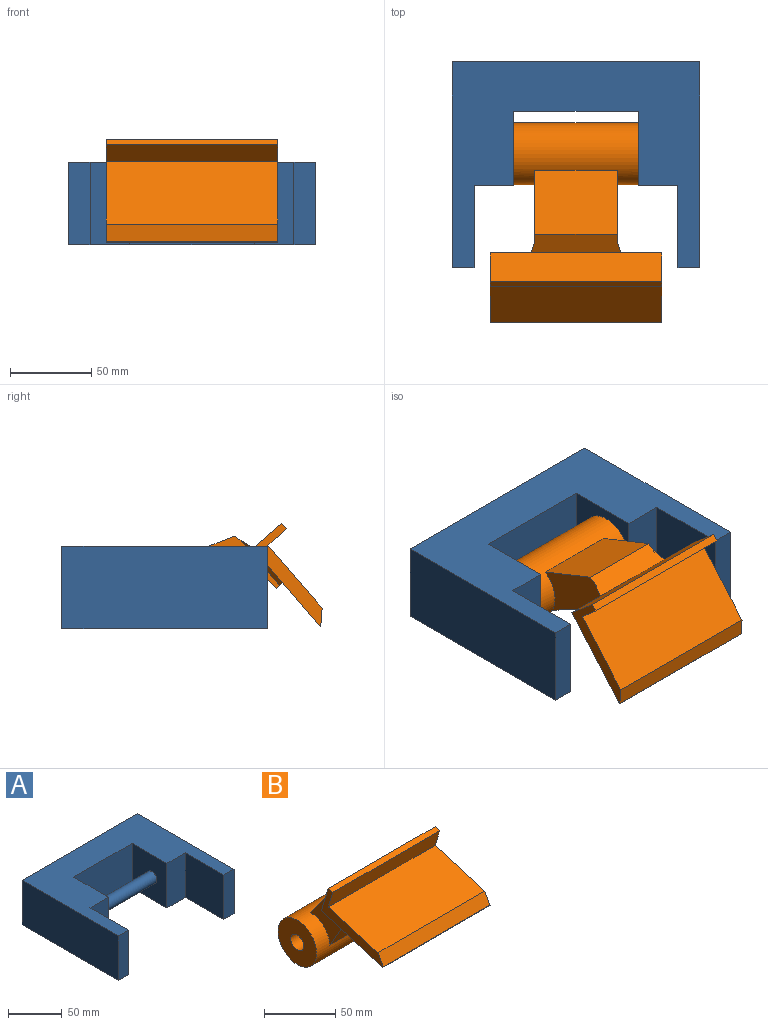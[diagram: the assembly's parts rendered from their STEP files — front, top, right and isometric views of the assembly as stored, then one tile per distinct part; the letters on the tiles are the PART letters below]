
ASSEMBLY  parts=2 mates=1
PART A: 15 faces, bbox 152.4x127x50.8 mm
  f0: plane 50.8x13.32mm, normal (0,-1,0), area 676.4mm2, adj f4,f8,f9,f14
  f1: plane 50.8x13.32mm, normal (0,-1,0), area 676.4mm2, adj f2,f8,f9,f11
  f2: plane 127x50.8mm, normal (1,0,0), area 6451.6mm2, adj f1,f3,f8,f9
  f3: plane 152.4x50.8mm, normal (0,1,0), area 7741.9mm2, adj f2,f4,f8,f9
  f4: plane 127x50.8mm, normal (-1,0,0), area 6451.6mm2, adj f0,f3,f8,f9
  f5: plane 50.8x45.86mm, normal (1,0,0), area 2203.1mm2, adj f6,f8,f9,f10,f13
  f6: plane 77x50.8mm, normal (0,-1,0), area 3911.4mm2, adj f5,f7,f8,f9
  f7: plane 50.8x45.86mm, normal (-1,0,0), area 2203.1mm2, adj f6,f8,f9,f10,f12
  f8: plane 152.4x127mm, normal (0,0,1), area 9444.2mm2, adj f0,f1,f2,f3,f4,f5,f6,f7
  f9: plane 152.4x127mm, normal (0,0,-1), area 9444.2mm2, adj f0,f1,f2,f3,f4,f5,f6,f7
  f10: cylinder r=6.35mm len=77mm, axis (-1,0,0), area 3072mm2, adj f5,f7
  f11: plane 50.8x50.72mm, normal (-1,0,0), area 2576.7mm2, adj f1,f8,f9,f12
  f12: plane 50.8x24.39mm, normal (0,-1,0), area 1238.8mm2, adj f7,f8,f9,f11
  f13: plane 50.8x24.39mm, normal (0,-1,0), area 1238.8mm2, adj f5,f8,f9,f14
  f14: plane 50.8x50.72mm, normal (1,0,0), area 2576.7mm2, adj f0,f8,f9,f13
PART B: 22 faces, bbox 105.8x118.4x95 mm
  f0: plane 55.88x13.95mm, normal (0,0,1), area 731.4mm2, adj f2,f3,f9,f16,f17,f18
  f1: plane 55.88x5.04mm, normal (0,-0.96,-0.29), area 273.6mm2, adj f2,f3,f10,f16,f17,f18
  f2: plane 64.52x52.9mm, normal (1,0,0), area 1136.4mm2, adj f0,f1,f5,f8,f9,f10,f17
  f3: plane 64.52x52.9mm, normal (-1,0,0), area 1136.4mm2, adj f0,f1,f5,f8,f9,f10,f18
  f4: cylinder r=6.35mm len=76.99mm, axis (-1,0,0), area 3071.7mm2, adj f6,f7
  f5: cylinder r=19.05mm len=76.99mm, axis (-1,0,0), area 7729.7mm2, adj f2,f3,f6,f7,f8,f9
  f6: plane 38.1x38.1mm, normal (1,0,0), area 1013.4mm2, adj f4,f5
  f7: plane 38.1x38.1mm, normal (-1,0,0), area 1013.4mm2, adj f4,f5
  f8: plane 50.8x43.18mm, normal (0,-0.87,-0.5), area 2526.2mm2, adj f2,f3,f5,f10
  f9: plane 50.8x34.46mm, normal (0,0.81,0.58), area 2149.3mm2, adj f0,f2,f3,f5
  f10: plane 50.8x20.12mm, normal (0,0.16,-0.99), area 1035.5mm2, adj f1,f2,f3,f8
  f11: plane 61x40.53mm, normal (1,0,0), area 557.8mm2, adj f12,f14,f15,f16,f19,f20,f21
  f12: plane 105.76x22.4mm, normal (0,0.96,0.29), area 2471.5mm2, adj f11,f13,f16,f20
  f13: plane 61x40.53mm, normal (-1,0,0), area 557.8mm2, adj f12,f14,f15,f16,f19,f20,f21
  f14: plane 105.76x0.49mm, normal (0,-0.96,-0.29), area 53.7mm2, adj f11,f13,f16,f21
  f15: plane 105.76x49.11mm, normal (0,-0.29,0.96), area 5419.4mm2, adj f11,f13,f19,f21
  f16: plane 105.76x60.86mm, normal (0,0.29,-0.96), area 5156.7mm2, adj f0,f1,f11,f12,f13,f14,f17,f18
  f17: plane 35.64x10.4mm, normal (0.71,0.2,-0.68), area 115.6mm2, adj f0,f1,f2,f16
  f18: plane 35.64x10.4mm, normal (-0.71,0.2,-0.68), area 115.6mm2, adj f0,f1,f3,f16
  f19: plane 105.76x14.61mm, normal (0,-0.96,-0.29), area 1611.8mm2, adj f11,f13,f15,f20
  f20: plane 105.76x4.45mm, normal (0,-0.29,0.96), area 490.7mm2, adj f11,f12,f13,f19
  f21: plane 105.76x9.48mm, normal (0,-0.88,0.48), area 1139.7mm2, adj f11,f13,f14,f15
PLACE A t=(-1.44,-53.46,-36.27)mm fixed
PLACE B rot(axis=(1,0,0),32.7deg) t=(-1.44,-46.59,-10.87)mm
MATE revolute A.f10 <-> B.f5  axis (-1,0,0) through (-1.44,-46.59,-10.87)mm
